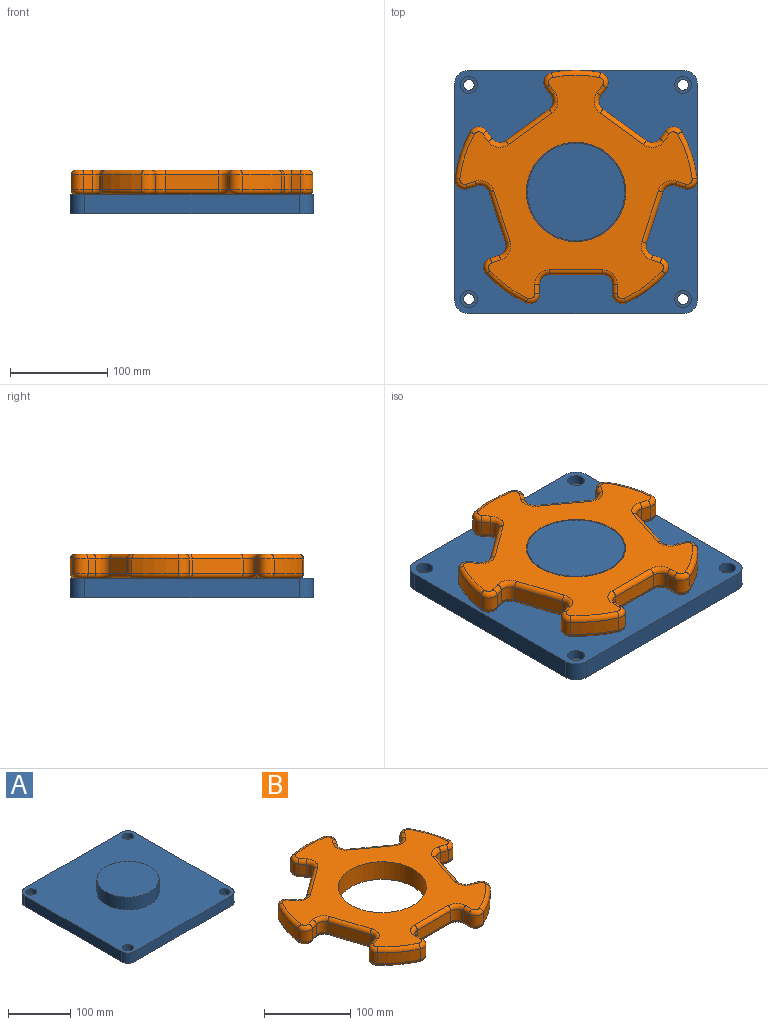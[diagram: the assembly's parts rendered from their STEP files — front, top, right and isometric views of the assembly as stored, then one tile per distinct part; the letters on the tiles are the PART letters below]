
ASSEMBLY  parts=2 mates=1
PART A: 24 faces, bbox 250x250x45 mm
  f0: plane 220x20mm, normal (1,0,0), area 4400mm2, adj f4,f5,f8,f11
  f1: plane 220x20mm, normal (0,1,0), area 4400mm2, adj f4,f5,f8,f9
  f2: plane 220x20mm, normal (-1,0,0), area 4400mm2, adj f4,f5,f9,f10
  f3: plane 220x20mm, normal (0,-1,0), area 4400mm2, adj f4,f5,f10,f11
  f4: plane 250x250mm, normal (0,0,1), area 53518.1mm2, adj f0,f1,f2,f3,f6,f8,f9,f10
  f5: plane 250x250mm, normal (0,0,-1), area 61926.7mm2, adj f0,f1,f2,f3,f8,f9,f10,f11
  f6: cylinder r=50mm len=100mm, axis (0,0,-1), area 7854mm2, adj f4,f7
  f7: plane 100x100mm, normal (0,0,1), area 7854mm2, adj f6
  f8: cylinder r=15mm len=20mm, axis (0,0,-1), area 471.2mm2, adj f0,f1,f4,f5
  f9: cylinder r=15mm len=20mm, axis (0,0,1), area 471.2mm2, adj f1,f2,f4,f5
  f10: cylinder r=15mm len=20mm, axis (0,0,-1), area 471.2mm2, adj f2,f3,f4,f5
  f11: cylinder r=15mm len=20mm, axis (0,0,1), area 471.2mm2, adj f0,f3,f4,f5
  f12: cylinder r=5.5mm len=11mm, axis (0,0,1), area 345.6mm2, adj f5,f13
  f13: plane 17.25x17.25mm, normal (0,0,1), area 138.7mm2, adj f12,f14
  f14: cylinder r=8.62mm len=17.25mm, axis (0,0,1), area 541.9mm2, adj f4,f13
  f15: cylinder r=5.5mm len=11mm, axis (0,0,1), area 345.6mm2, adj f5,f16
  f16: plane 17.25x17.25mm, normal (0,0,1), area 138.7mm2, adj f15,f17
  f17: cylinder r=8.62mm len=17.25mm, axis (0,0,1), area 541.9mm2, adj f4,f16
  f18: cylinder r=5.5mm len=11mm, axis (0,0,1), area 345.6mm2, adj f5,f19
  f19: plane 17.25x17.25mm, normal (0,0,1), area 138.7mm2, adj f18,f20
  f20: cylinder r=8.62mm len=17.25mm, axis (0,0,1), area 541.9mm2, adj f4,f19
  f21: cylinder r=5.5mm len=11mm, axis (0,0,1), area 345.6mm2, adj f5,f22
  f22: plane 17.25x17.25mm, normal (0,0,1), area 138.7mm2, adj f21,f23
  f23: cylinder r=8.62mm len=17.25mm, axis (0,0,1), area 541.9mm2, adj f4,f22
PART B: 123 faces, bbox 268.9x258.5x25 mm
  f0: plane 238.57x229.73mm, normal (0,0,1), area 21505.7mm2, adj f6,f43,f44,f45,f46,f47,f48,f49
  f1: plane 238.57x229.73mm, normal (0,0,-1), area 21505.7mm2, adj f6,f83,f84,f85,f86,f87,f88,f89
  f2: cylinder r=125mm len=40.68mm, axis (0,0,-1), area 759.5mm2, adj f13,f42,f51,f91
  f3: cylinder r=125mm len=47.82mm, axis (0,0,-1), area 759.5mm2, adj f35,f41,f67,f107
  f4: cylinder r=125mm len=50.29mm, axis (0,0,-1), area 759.5mm2, adj f28,f34,f82,f122
  f5: cylinder r=125mm len=47.82mm, axis (0,0,-1), area 759.5mm2, adj f21,f27,f66,f106
  f6: cylinder r=51mm len=102mm, axis (0,0,-1), area 8011.1mm2, adj f0,f1
  f7: cylinder r=125mm len=40.68mm, axis (0,0,-1), area 759.5mm2, adj f14,f20,f50,f90
  f8: plane 15x9.73mm, normal (-1,0,0), area 146mm2, adj f11,f14,f46,f86
  f9: plane 55x15mm, normal (0,-1,0), area 825mm2, adj f11,f12,f43,f83
  f10: plane 15x9.73mm, normal (1,0,0), area 146mm2, adj f12,f13,f47,f87
  f11: cylinder r=10mm len=15mm, axis (0,0,-1), area 235.6mm2, adj f8,f9,f44,f84
  f12: cylinder r=10mm len=15mm, axis (0,0,-1), area 235.6mm2, adj f9,f10,f45,f85
  f13: cylinder r=10mm len=15mm, axis (0,0,-1), area 299.5mm2, adj f2,f10,f49,f89
  f14: cylinder r=10mm len=15mm, axis (0,0,-1), area 299.5mm2, adj f7,f8,f48,f88
  f15: plane 15x9.26mm, normal (-0.31,-0.95,0), area 146mm2, adj f18,f21,f62,f102
  f16: plane 52.31x17mm, normal (0.95,-0.31,0), area 825mm2, adj f18,f19,f58,f98
  f17: plane 15x9.26mm, normal (0.31,0.95,0), area 146mm2, adj f19,f20,f54,f94
  f18: cylinder r=10mm len=15mm, axis (0,0,-1), area 235.6mm2, adj f15,f16,f60,f100
  f19: cylinder r=10mm len=15mm, axis (0,0,-1), area 235.6mm2, adj f16,f17,f56,f96
  f20: cylinder r=10mm len=16.25mm, axis (0,0,-1), area 299.5mm2, adj f7,f17,f52,f92
  f21: cylinder r=10mm len=15mm, axis (0,0,-1), area 299.5mm2, adj f5,f15,f64,f104
  f22: plane 15x7.87mm, normal (0.81,-0.59,0), area 146mm2, adj f25,f28,f78,f118
  f23: plane 44.5x32.33mm, normal (0.59,0.81,0), area 825mm2, adj f25,f26,f74,f114
  f24: plane 15x7.87mm, normal (-0.81,0.59,0), area 146mm2, adj f26,f27,f70,f110
  f25: cylinder r=10mm len=15mm, axis (0,0,-1), area 235.6mm2, adj f22,f23,f76,f116
  f26: cylinder r=10mm len=15mm, axis (0,0,-1), area 235.6mm2, adj f23,f24,f72,f112
  f27: cylinder r=10mm len=16.78mm, axis (0,0,-1), area 299.5mm2, adj f5,f24,f68,f108
  f28: cylinder r=10mm len=15.67mm, axis (0,0,-1), area 299.5mm2, adj f4,f22,f80,f120
  f29: plane 15x7.87mm, normal (0.81,0.59,0), area 146mm2, adj f32,f35,f71,f111
  f30: plane 44.5x32.33mm, normal (-0.59,0.81,0), area 825mm2, adj f32,f33,f75,f115
  f31: plane 15x7.87mm, normal (-0.81,-0.59,0), area 146mm2, adj f33,f34,f79,f119
  f32: cylinder r=10mm len=15mm, axis (0,0,-1), area 235.6mm2, adj f29,f30,f73,f113
  f33: cylinder r=10mm len=15mm, axis (0,0,-1), area 235.6mm2, adj f30,f31,f77,f117
  f34: cylinder r=10mm len=15.67mm, axis (0,0,-1), area 299.5mm2, adj f4,f31,f81,f121
  f35: cylinder r=10mm len=16.78mm, axis (0,0,-1), area 299.5mm2, adj f3,f29,f69,f109
  f36: plane 15x9.26mm, normal (-0.31,0.95,0), area 146mm2, adj f39,f42,f55,f95
  f37: plane 52.31x17mm, normal (-0.95,-0.31,0), area 825mm2, adj f39,f40,f59,f99
  f38: plane 15x9.26mm, normal (0.31,-0.95,0), area 146mm2, adj f40,f41,f63,f103
  f39: cylinder r=10mm len=15mm, axis (0,0,-1), area 235.6mm2, adj f36,f37,f57,f97
  f40: cylinder r=10mm len=15mm, axis (0,0,-1), area 235.6mm2, adj f37,f38,f61,f101
  f41: cylinder r=10mm len=15mm, axis (0,0,-1), area 299.5mm2, adj f3,f38,f65,f105
  f42: cylinder r=10mm len=16.25mm, axis (0,0,-1), area 299.5mm2, adj f2,f36,f53,f93
  f43: cylinder r=5mm len=55mm, axis (1,0,0), area 432mm2, adj f0,f9,f44,f45
  f44: torus R=15mm, axis (0,0,1), area 145.8mm2, adj f0,f11,f43,f46
  f45: torus R=15mm, axis (0,0,1), area 145.8mm2, adj f0,f12,f43,f47
  f46: cylinder r=5mm len=9.73mm, axis (0,-1,0), area 76.4mm2, adj f0,f8,f44,f48
  f47: cylinder r=5mm len=9.73mm, axis (0,1,0), area 76.4mm2, adj f0,f10,f45,f49
  f48: torus R=5mm, axis (0,0,1), area 128.3mm2, adj f0,f14,f46,f50
  f49: torus R=5mm, axis (0,0,1), area 128.3mm2, adj f0,f13,f47,f51
  f50: torus R=120mm, axis (0,0,1), area 391.9mm2, adj f0,f7,f48,f52
  f51: torus R=120mm, axis (0,0,1), area 391.9mm2, adj f0,f2,f49,f53
  f52: torus R=5mm, axis (0,0,1), area 128.3mm2, adj f0,f20,f50,f54
  f53: torus R=5mm, axis (0,0,1), area 128.3mm2, adj f0,f42,f51,f55
  f54: cylinder r=5mm len=10.8mm, axis (-0.95,0.31,0), area 76.4mm2, adj f0,f17,f52,f56
  f55: cylinder r=5mm len=10.8mm, axis (-0.95,-0.31,0), area 76.4mm2, adj f0,f36,f53,f57
  f56: torus R=15mm, axis (0,0,1), area 145.8mm2, adj f0,f19,f54,f58
  f57: torus R=15mm, axis (0,0,1), area 145.8mm2, adj f0,f39,f55,f59
  f58: cylinder r=5mm len=53.85mm, axis (0.31,0.95,0), area 432mm2, adj f0,f16,f56,f60
  f59: cylinder r=5mm len=53.85mm, axis (0.31,-0.95,0), area 432mm2, adj f0,f37,f57,f61
  f60: torus R=15mm, axis (0,0,1), area 145.8mm2, adj f0,f18,f58,f62
  f61: torus R=15mm, axis (0,0,1), area 145.8mm2, adj f0,f40,f59,f63
  f62: cylinder r=5mm len=10.8mm, axis (0.95,-0.31,0), area 76.4mm2, adj f0,f15,f60,f64
  f63: cylinder r=5mm len=10.8mm, axis (0.95,0.31,0), area 76.4mm2, adj f0,f38,f61,f65
  f64: torus R=5mm, axis (0,0,1), area 128.3mm2, adj f0,f21,f62,f66
  f65: torus R=5mm, axis (0,0,1), area 128.3mm2, adj f0,f41,f63,f67
  f66: torus R=120mm, axis (0,0,1), area 391.9mm2, adj f0,f5,f64,f68
  f67: torus R=120mm, axis (0,0,1), area 391.9mm2, adj f0,f3,f65,f69
  f68: torus R=5mm, axis (0,0,1), area 128.3mm2, adj f0,f27,f66,f70
  f69: torus R=5mm, axis (0,0,1), area 128.3mm2, adj f0,f35,f67,f71
  f70: cylinder r=5mm len=10.81mm, axis (-0.59,-0.81,0), area 76.4mm2, adj f0,f24,f68,f72
  f71: cylinder r=5mm len=10.81mm, axis (-0.59,0.81,0), area 76.4mm2, adj f0,f29,f69,f73
  f72: torus R=15mm, axis (0,0,1), area 145.8mm2, adj f0,f26,f70,f74
  f73: torus R=15mm, axis (0,0,1), area 145.8mm2, adj f0,f32,f71,f75
  f74: cylinder r=5mm len=47.44mm, axis (-0.81,0.59,0), area 432mm2, adj f0,f23,f72,f76
  f75: cylinder r=5mm len=47.44mm, axis (-0.81,-0.59,0), area 432mm2, adj f0,f30,f73,f77
  f76: torus R=15mm, axis (0,0,1), area 145.8mm2, adj f0,f25,f74,f78
  f77: torus R=15mm, axis (0,0,1), area 145.8mm2, adj f0,f33,f75,f79
  f78: cylinder r=5mm len=10.81mm, axis (0.59,0.81,0), area 76.4mm2, adj f0,f22,f76,f80
  f79: cylinder r=5mm len=10.81mm, axis (0.59,-0.81,0), area 76.4mm2, adj f0,f31,f77,f81
  f80: torus R=5mm, axis (0,0,1), area 128.3mm2, adj f0,f28,f78,f82
  f81: torus R=5mm, axis (0,0,1), area 128.3mm2, adj f0,f34,f79,f82
  f82: torus R=120mm, axis (0,0,1), area 391.9mm2, adj f0,f4,f80,f81
  f83: cylinder r=5mm len=55mm, axis (-1,0,0), area 432mm2, adj f1,f9,f84,f85
  f84: torus R=15mm, axis (0,0,1), area 145.8mm2, adj f1,f11,f83,f86
  f85: torus R=15mm, axis (0,0,1), area 145.8mm2, adj f1,f12,f83,f87
  f86: cylinder r=5mm len=9.73mm, axis (0,1,0), area 76.4mm2, adj f1,f8,f84,f88
  f87: cylinder r=5mm len=9.73mm, axis (0,-1,0), area 76.4mm2, adj f1,f10,f85,f89
  f88: torus R=5mm, axis (0,0,1), area 128.3mm2, adj f1,f14,f86,f90
  f89: torus R=5mm, axis (0,0,1), area 128.3mm2, adj f1,f13,f87,f91
  f90: torus R=120mm, axis (0,0,1), area 391.9mm2, adj f1,f7,f88,f92
  f91: torus R=120mm, axis (0,0,1), area 391.9mm2, adj f1,f2,f89,f93
  f92: torus R=5mm, axis (0,0,1), area 128.3mm2, adj f1,f20,f90,f94
  f93: torus R=5mm, axis (0,0,1), area 128.3mm2, adj f1,f42,f91,f95
  f94: cylinder r=5mm len=10.8mm, axis (0.95,-0.31,0), area 76.4mm2, adj f1,f17,f92,f96
  f95: cylinder r=5mm len=10.8mm, axis (0.95,0.31,0), area 76.4mm2, adj f1,f36,f93,f97
  f96: torus R=15mm, axis (0,0,1), area 145.8mm2, adj f1,f19,f94,f98
  f97: torus R=15mm, axis (0,0,1), area 145.8mm2, adj f1,f39,f95,f99
  f98: cylinder r=5mm len=53.85mm, axis (-0.31,-0.95,0), area 432mm2, adj f1,f16,f96,f100
  f99: cylinder r=5mm len=53.85mm, axis (-0.31,0.95,0), area 432mm2, adj f1,f37,f97,f101
  f100: torus R=15mm, axis (0,0,1), area 145.8mm2, adj f1,f18,f98,f102
  f101: torus R=15mm, axis (0,0,1), area 145.8mm2, adj f1,f40,f99,f103
  f102: cylinder r=5mm len=10.8mm, axis (-0.95,0.31,0), area 76.4mm2, adj f1,f15,f100,f104
  f103: cylinder r=5mm len=10.8mm, axis (-0.95,-0.31,0), area 76.4mm2, adj f1,f38,f101,f105
  f104: torus R=5mm, axis (0,0,1), area 128.3mm2, adj f1,f21,f102,f106
  f105: torus R=5mm, axis (0,0,1), area 128.3mm2, adj f1,f41,f103,f107
  f106: torus R=120mm, axis (0,0,1), area 391.9mm2, adj f1,f5,f104,f108
  f107: torus R=120mm, axis (0,0,1), area 391.9mm2, adj f1,f3,f105,f109
  f108: torus R=5mm, axis (0,0,1), area 128.3mm2, adj f1,f27,f106,f110
  f109: torus R=5mm, axis (0,0,1), area 128.3mm2, adj f1,f35,f107,f111
  f110: cylinder r=5mm len=10.81mm, axis (0.59,0.81,0), area 76.4mm2, adj f1,f24,f108,f112
  f111: cylinder r=5mm len=10.81mm, axis (0.59,-0.81,0), area 76.4mm2, adj f1,f29,f109,f113
  f112: torus R=15mm, axis (0,0,1), area 145.8mm2, adj f1,f26,f110,f114
  f113: torus R=15mm, axis (0,0,1), area 145.8mm2, adj f1,f32,f111,f115
  f114: cylinder r=5mm len=47.44mm, axis (0.81,-0.59,0), area 432mm2, adj f1,f23,f112,f116
  f115: cylinder r=5mm len=47.44mm, axis (0.81,0.59,0), area 432mm2, adj f1,f30,f113,f117
  f116: torus R=15mm, axis (0,0,1), area 145.8mm2, adj f1,f25,f114,f118
  f117: torus R=15mm, axis (0,0,1), area 145.8mm2, adj f1,f33,f115,f119
  f118: cylinder r=5mm len=10.81mm, axis (-0.59,-0.81,0), area 76.4mm2, adj f1,f22,f116,f120
  f119: cylinder r=5mm len=10.81mm, axis (-0.59,0.81,0), area 76.4mm2, adj f1,f31,f117,f121
  f120: torus R=5mm, axis (0,0,1), area 128.3mm2, adj f1,f28,f118,f122
  f121: torus R=5mm, axis (0,0,1), area 128.3mm2, adj f1,f34,f119,f122
  f122: torus R=120mm, axis (0,0,1), area 391.9mm2, adj f1,f4,f120,f121
PLACE A at identity fixed
PLACE B at identity
MATE revolute A.f6 <-> B.f2  axis (0,0,1) through (0,0,45)mm
